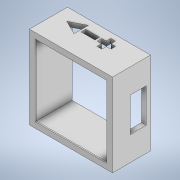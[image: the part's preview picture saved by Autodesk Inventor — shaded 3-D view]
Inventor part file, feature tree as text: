
AUTODESK INVENTOR PART (.ipt)
format: ipt  version: 2020.1 (Build 241239000, 239)  size: 219,136 bytes
history: native  units: in
note: dims shown in document units (in); Inventor stores cm internally (conversion verified against a paired STEP export)
features: extrude x9, sketch x8
ambient origin geometry x8: Origin, YZ Plane, XZ Plane, XY Plane, X Axis, Y Axis, Z Axis, Center Point
bodies: Solid1 (feature_tree)
feature tree (17):
  extrude  "Extrusion1"  Depth=2.874in
  extrude  "Extrusion2"  Depth=0.1575in
  extrude  "Extrusion3"  Depth=0.0394in
  extrude  "Extrusion4"  Depth=0.0394in TaperAngle=0.0deg
  extrude  "Extrusion5"  Depth=0.5512in
  extrude  "Extrusion6"  Depth=0.1575in TaperAngle=0.0deg
  extrude  "Extrusion7"  Depth=0.0787in
  sketch  "Sketch10"  dims[d56=0.1181in d57=0.0984in d58=0.0in d93=0.1575in d94=0.0in d95=0.0039in d96=0.0039in d97=0.0039in d98=0.1575in d99=0.0in d42=0.0197in]
  extrude  "Extrusion8"  Depth=0.0984in TaperAngle=0.0deg
  extrude  "Extrusion9"  Depth=0.1575in TaperAngle=0.0deg
  sketch  "Sketch2"  dims[d2=2.874in d3=2.874in]
  sketch  "Sketch3"  dims[d4=0.7874in d5=0.0in d6=0.1575in]
  sketch  "Sketch4"  dims[d7=0.7874in d8=0.0in d9=0.0394in]
  sketch  "Sketch5"  dims[d10=0.0394in d11=0.0in d12=0.5315in d13=0.0in]
  sketch  "Sketch7"  dims[d43=0.5906in d44=0.5512in]
  sketch  "Sketch8"  dims[d45=1.1811in d46=0.1575in d47=0.0in]
  sketch  "Sketch9"  dims[d53=0.1575in d54=0.0in d55=0.0787in]
